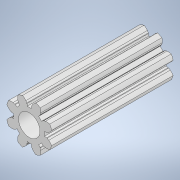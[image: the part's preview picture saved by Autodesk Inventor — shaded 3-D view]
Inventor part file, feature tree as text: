
AUTODESK INVENTOR PART (.ipt)
format: ipt  version: 2022.2 (Build 262287010, 287A)  size: 236,032 bytes
history: native  units: mm
features: extrude x1, sketch x1
ambient origin geometry x8: Origin, YZ Plane, XZ Plane, XY Plane, X Axis, Y Axis, Z Axis, Center Point
bodies: Body1 (feature_tree)
feature tree (2):
  extrude  "Extrusion2"  Depth=13.0mm
  sketch  "Sketch2"  dims[d3=13.0mm d4=0.0mm d6=2.3mm]
